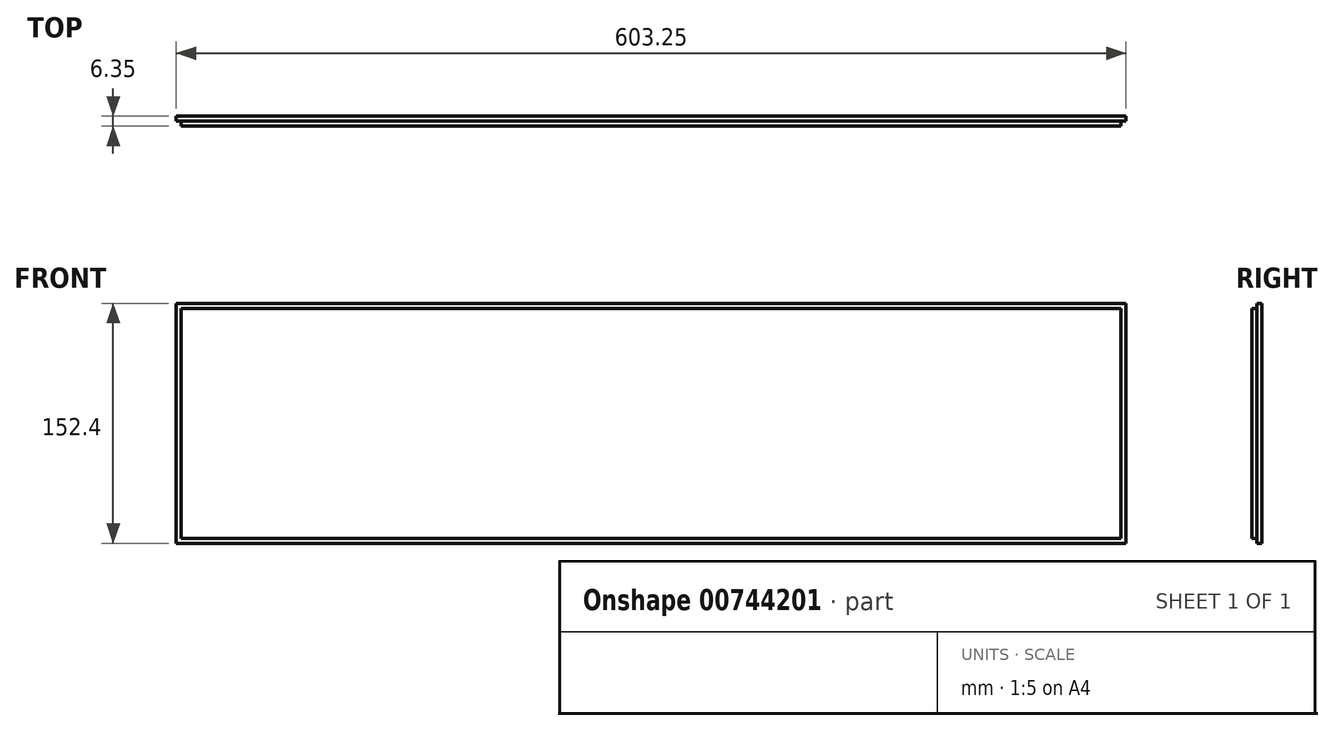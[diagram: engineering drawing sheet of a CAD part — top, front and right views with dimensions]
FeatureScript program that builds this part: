
annotation { "Feature Type Name" : "Feature", "Feature Type Description" : "" }
export const myFeature = defineFeature(function(context is Context, id is Id, definition is map)
    precondition{}
    {
        {
            var Q0;
            Q0=qCreatedBy(makeId("Front.planeOp"),FACE);
            var sketch = newSketch(context, id + "F0", { "sketchPlane" : qUnion([Q0])});
            skLineSegment(sketch, "E0.bottom", {"start": v(-298.45, 76.2) * mm, "end": v(298.45, 76.2) * mm});
            skLineSegment(sketch, "E0.top", {"start": v(-298.45, -76.2) * mm, "end": v(298.45, -76.2) * mm});
            skLineSegment(sketch, "E0.left", {"start": v(-298.45, 76.2) * mm, "end": v(-298.45, -76.2) * mm});
            skLineSegment(sketch, "E0.right", {"start": v(298.45, 76.2) * mm, "end": v(298.45, -76.2) * mm});
            skLineSegment(sketch, "E1", {"start": v(-298.45, 0) * mm, "end": v(298.45, 0) * mm, "construction": true});
            skLineSegment(sketch, "E2", {"start": v(0, 76.2) * mm, "end": v(0, -76.2) * mm, "construction": true});
            skSolve(sketch);
        }
        {
            var Q0;
            Q0 = qSketchRegion(id + "F0", true);
            extrude(context, id + "F1", {"entities" : qUnion([Q0]), "depth" : 6.35 * mm, "offsetDistance" : 25.4 * mm});
        }
        {
            var Q0;
            Q0=makeQuery(id+"F1.opExtrude","SWEPT_FACE",FACE,{"disambiguationData":[OSD([sQuery(id+"F0.wireOp",EDGE,"E0.right")])]});
            var sketch = newSketch(context, id + "F2", { "sketchPlane" : qUnion([Q0])});
            skLineSegment(sketch, "E3.bottom", {"start": v(-6.35, 76.2) * mm, "end": v(-3.18, 76.2) * mm});
            skLineSegment(sketch, "E3.top", {"start": v(-6.35, 73.03) * mm, "end": v(-3.18, 73.03) * mm});
            skLineSegment(sketch, "E3.left", {"start": v(-6.35, 76.2) * mm, "end": v(-6.35, 73.03) * mm});
            skLineSegment(sketch, "E3.right", {"start": v(-3.18, 76.2) * mm, "end": v(-3.18, 73.03) * mm});
            skLineSegment(sketch, "E4.bottom", {"start": v(-6.35, -76.2) * mm, "end": v(-3.17, -76.2) * mm});
            skLineSegment(sketch, "E4.top", {"start": v(-6.35, -73.03) * mm, "end": v(-3.18, -73.03) * mm});
            skLineSegment(sketch, "E4.left", {"start": v(-6.35, -76.2) * mm, "end": v(-6.35, -73.03) * mm});
            skLineSegment(sketch, "E4.right", {"start": v(-3.17, -76.2) * mm, "end": v(-3.18, -73.03) * mm});
            skSolve(sketch);
        }
        {
            var Q0;
            Q0=makeQuery(id+"F2.imprint","IMPRINT",FACE,{"disambiguationData":[TD([[makeQuery(id+"F2.imprint","IMPRINT",EDGE,{"derivedFrom":sQuery(id+"F2.wireOp",EDGE,"E4.bottom")}),1.0]])]});
            var Q1;
            Q1=makeQuery(id+"F2.imprint","IMPRINT",FACE,{"disambiguationData":[TD([[makeQuery(id+"F2.imprint","IMPRINT",EDGE,{"derivedFrom":sQuery(id+"F2.wireOp",EDGE,"E3.bottom")}),-1.0]])]});
            extrude(context, id + "F3", {"entities" : qUnion([Q0, Q1]), "operationType" : NewBodyOperationType.REMOVE, "endBound" : BoundingType.THROUGH_ALL, "oppositeDirection" : true, "depth" : 25.4 * mm, "offsetDistance" : 25.4 * mm});
        }
        {
            var Q0;
            Q0=makeQuery(id+"F1.opExtrude","SWEPT_FACE",FACE,{"disambiguationData":[OSD([sQuery(id+"F0.wireOp",EDGE,"E0.bottom")])]});
            var sketch = newSketch(context, id + "F4", { "sketchPlane" : qUnion([Q0])});
            skLineSegment(sketch, "E5.bottom", {"start": v(298.45, -3.18) * mm, "end": v(301.63, -3.18) * mm});
            skLineSegment(sketch, "E5.top", {"start": v(298.45, 0) * mm, "end": v(301.63, 0) * mm});
            skLineSegment(sketch, "E5.left", {"start": v(298.45, -3.18) * mm, "end": v(298.45, 0) * mm});
            skLineSegment(sketch, "E5.right", {"start": v(301.63, -3.18) * mm, "end": v(301.63, 0) * mm});
            skLineSegment(sketch, "E6.bottom", {"start": v(-298.45, -3.18) * mm, "end": v(-301.63, -3.18) * mm});
            skLineSegment(sketch, "E6.top", {"start": v(-298.45, 0) * mm, "end": v(-301.63, 0) * mm});
            skLineSegment(sketch, "E6.left", {"start": v(-298.45, -3.18) * mm, "end": v(-298.45, 0) * mm});
            skLineSegment(sketch, "E6.right", {"start": v(-301.63, -3.18) * mm, "end": v(-301.63, 0) * mm});
            skSolve(sketch);
        }
        {
            var Q0;
            Q0=makeQuery(id+"F4.imprint","IMPRINT",FACE,{"disambiguationData":[TD([[makeQuery(id+"F4.imprint","IMPRINT",EDGE,{"derivedFrom":sQuery(id+"F4.wireOp",EDGE,"E6.bottom")}),-1.0]])]});
            var Q1;
            Q1=makeQuery(id+"F4.imprint","IMPRINT",FACE,{"disambiguationData":[TD([[makeQuery(id+"F4.imprint","IMPRINT",EDGE,{"derivedFrom":sQuery(id+"F4.wireOp",EDGE,"E5.bottom")}),1.0]])]});
            var Q2;
            Q2=makeQuery(id+"F1.opExtrude","SWEPT_FACE",FACE,{"disambiguationData":[OSD([sQuery(id+"F0.wireOp",EDGE,"E0.top")])]});
            extrude(context, id + "F5", {"entities" : qUnion([Q0, Q1]), "operationType" : NewBodyOperationType.ADD, "endBound" : BoundingType.UP_TO_SURFACE, "oppositeDirection" : true, "depth" : 25.4 * mm, "endBoundEntityFace" : qUnion([Q2]), "offsetDistance" : 25.4 * mm});
        }
    });
